# Revit family: Faucet-Lavatory-KOHLER-July-K-16027IN_1
name_source: partatom
category: Plumbing Fixtures
revit_build: Autodesk Revit 2017 (Build: 20160225_1515(x64)
units: mm (PartAtom-declared; Revit-internal decimal feet)

## family parameters
Cut with Voids When Loaded = No
Host = Face
OmniClass Number = 23.31.11.00
OmniClass Title = Faucets
Part Type = Normal
Room Calculation Point = No
Round Connector Dimension = Use Diameter
Shared = No

## types (3) — shared parameters
ADA Compliant = No
Assembly Code = D2010
CW Connection = Yes
Cold Water Inlet = Cold Water Inlet
Date Modified = 08/27/2020
Default Elevation = 36"
Description = Single control lavatory faucet
Drain Included = No
Flow Rate = 0 GPM
HW Connection = Yes
Handle Clearance = 4 3/16"
Height = 4 1/2"
Hot Water Inlet = Hot Water Inlet
Length = 4 3/8"
Manufacturer = KOHLER Co.
Master Format 2014 = 22 41 39
Master Format 2014 Name = Residential Faucets, Supplies, and Trim
Material = Solid Brass Construction
Pressure = 0.00 psi
Product Documentation Link = http://resources.kohler.com
Product Name = July
Product Page URL = https://www.kohler.co.in
Spout Reach = 4 3/8"
URL = https://www.kohler.co.in
Vent Connection = No
Waste Connection = No
Waste Water Outlet = Waste Water Outlet
WaterSense Certified = No
Width = 1 7/8"

## per-type parameters (varying)
| type | Finish | Model | Type |
| CP-Polished Chrome | Kohler-Metal-CP-Polished_Chrome | K-16027IN-4ND-CP | 1 |
| BN-Vibrant Brushed Nickel | Kohler-Metal-BN-Vibrant_Brushed_Nickel | K-16027IN-4ND-BN | 2 |
| AF-Vibrant French Gold | Kohler-Metal-AF-Vibrant_French_Gold | K-16027IN-4ND-AF | 3 |

## geometry (parser evidence)
native form markers: Sweep x4
no freeform markers — native parametric forms only
